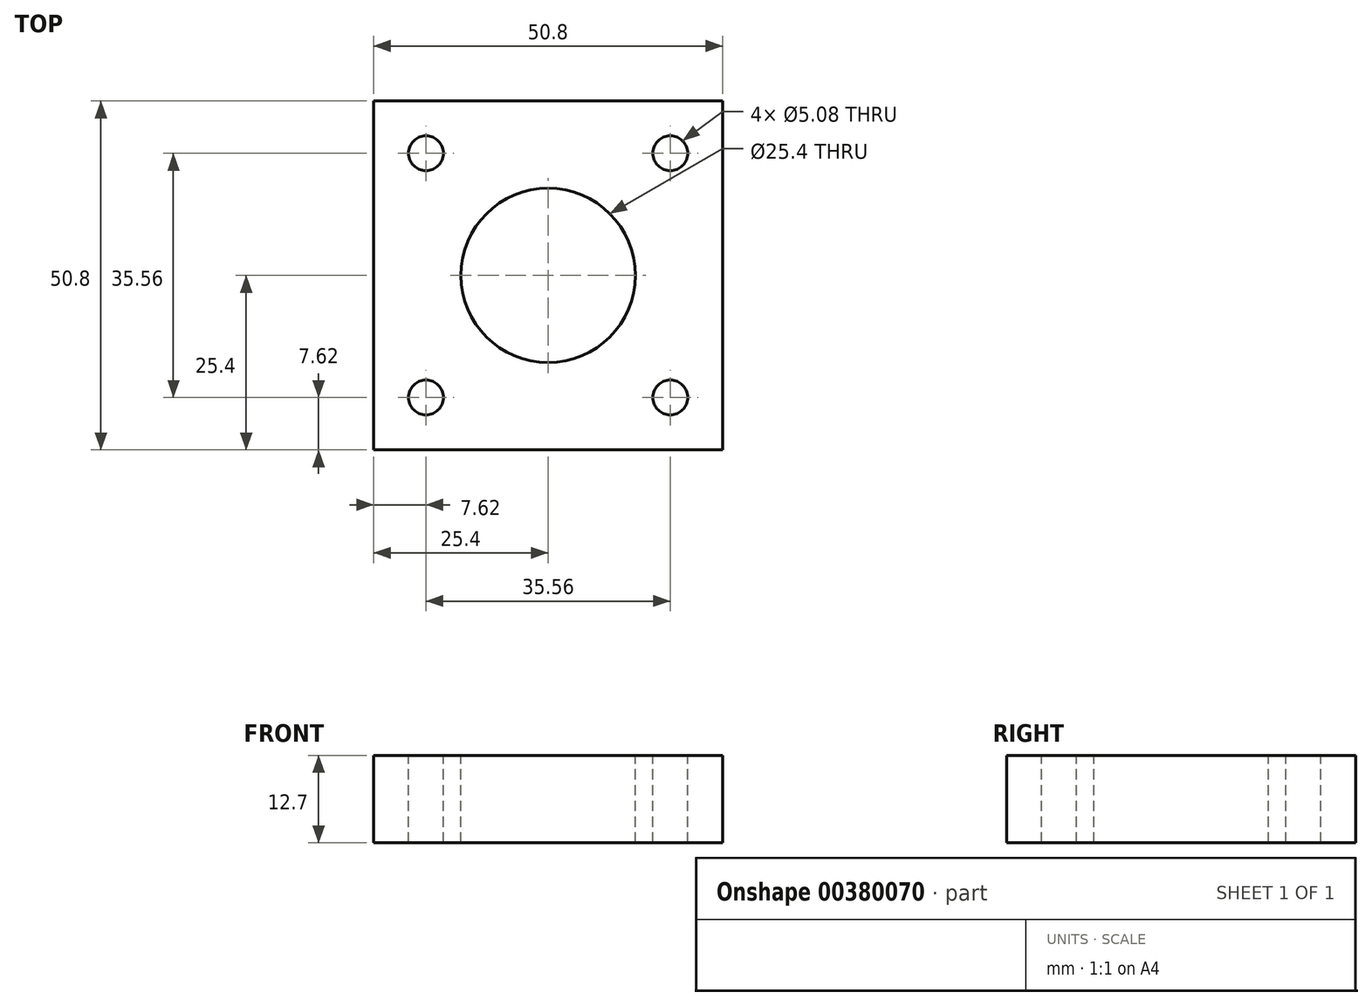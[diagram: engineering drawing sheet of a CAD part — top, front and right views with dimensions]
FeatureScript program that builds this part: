
annotation { "Feature Type Name" : "Feature", "Feature Type Description" : "" }
export const myFeature = defineFeature(function(context is Context, id is Id, definition is map)
    precondition{}
    {
        {
            var Q0;
            Q0=qCreatedBy(makeId("Top.planeOp"),FACE);
            var sketch = newSketch(context, id + "F0", { "sketchPlane" : qUnion([Q0])});
            skLineSegment(sketch, "E0.bottom", {"start": v(25.4, -25.4) * mm, "end": v(-25.4, -25.4) * mm});
            skLineSegment(sketch, "E0.top", {"start": v(25.4, 25.4) * mm, "end": v(-25.4, 25.4) * mm});
            skLineSegment(sketch, "E0.left", {"start": v(25.4, -25.4) * mm, "end": v(25.4, 25.4) * mm});
            skLineSegment(sketch, "E0.right", {"start": v(-25.4, -25.4) * mm, "end": v(-25.4, 25.4) * mm});
            skPoint(sketch, "E0.middle", {"position": v(0, 0) * mm});
            skSolve(sketch);
        }
        {
            var Q0;
            Q0=makeQuery(id+"F0.imprint","IMPRINT",FACE,{"disambiguationData":[TD([[makeQuery(id+"F0.imprint","IMPRINT",EDGE,{"derivedFrom":sQuery(id+"F0.wireOp",EDGE,"E0.bottom")}),-1.0]])]});
            extrude(context, id + "F1", {"entities" : qUnion([Q0]), "depth" : 12.7 * mm});
        }
        {
            var Q0;
            Q0=makeQuery(id+"F1.opExtrude","CAP_FACE",FACE,{"disambiguationData":[OSD([sQuery(id+"F0.wireOp",EDGE,"E0.bottom"),sQuery(id+"F0.wireOp",EDGE,"E0.top"),sQuery(id+"F0.wireOp",EDGE,"E0.left"),sQuery(id+"F0.wireOp",EDGE,"E0.right")])],"isStart":false});
            var sketch = newSketch(context, id + "F2", { "sketchPlane" : qUnion([Q0])});
            skCircle(sketch, "E1", {"center": v(17.78, 17.78) * mm, "radius": 2.54 * mm});
            skCircle(sketch, "E2", {"center": v(17.78, -17.78) * mm, "radius": 2.54 * mm});
            skCircle(sketch, "E3", {"center": v(-17.78, 17.78) * mm, "radius": 2.54 * mm});
            skCircle(sketch, "E4", {"center": v(-17.78, -17.78) * mm, "radius": 2.54 * mm});
            skCircle(sketch, "E5", {"center": v(0, 0) * mm, "radius": 12.7 * mm});
            skSolve(sketch);
        }
        {
            var Q0;
            Q0 = qSketchRegion(id + "F2", true);
            extrude(context, id + "F3", {"entities" : qUnion([Q0]), "operationType" : NewBodyOperationType.REMOVE, "oppositeDirection" : true, "depth" : 25.15 * mm});
        }
    });
